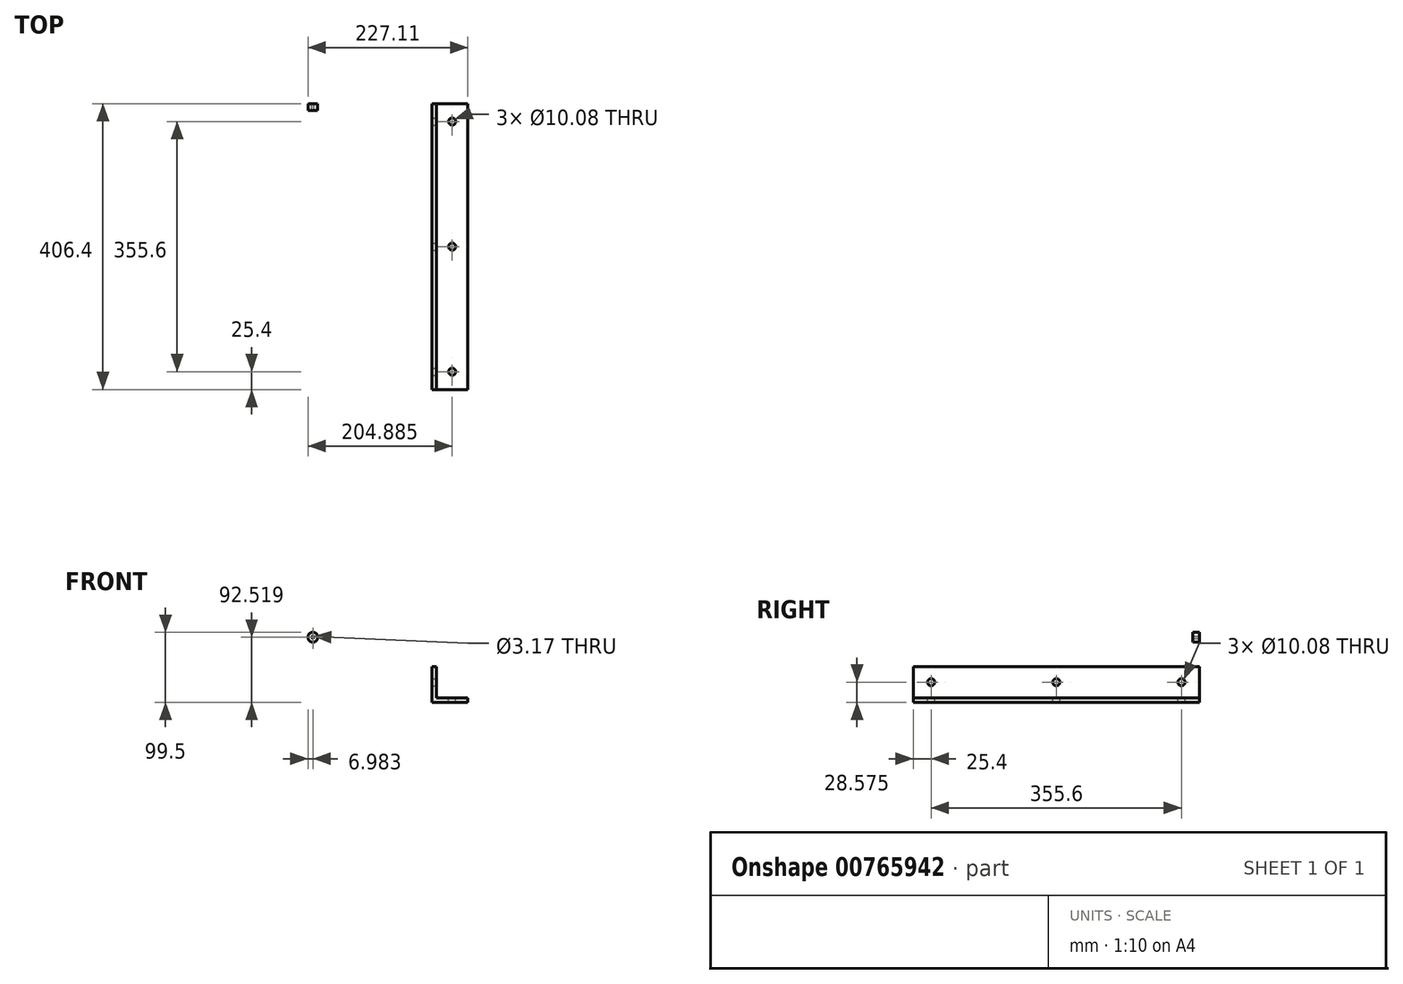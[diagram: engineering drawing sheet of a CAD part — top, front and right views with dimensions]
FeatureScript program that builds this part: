
annotation { "Feature Type Name" : "Feature", "Feature Type Description" : "" }
export const myFeature = defineFeature(function(context is Context, id is Id, definition is map)
    precondition{}
    {
        {
            var Q0;
            Q0=qCreatedBy(makeId("Front.planeOp"),FACE);
            var sketch = newSketch(context, id + "F0", { "sketchPlane" : qUnion([Q0])});
            skLineSegment(sketch, "E0", {"start": v(0, 0) * mm, "end": v(0, 50.8) * mm});
            skLineSegment(sketch, "E1", {"start": v(0, 50.8) * mm, "end": v(0, 50.8) * mm});
            skLineSegment(sketch, "E2", {"start": v(50.8, 6.35) * mm, "end": v(50.8, 0) * mm});
            skLineSegment(sketch, "E3", {"start": v(50.8, 0) * mm, "end": v(0, 0) * mm});
            skLineSegment(sketch, "E4", {"start": v(50.8, 6.35) * mm, "end": v(6.35, 6.35) * mm});
            skLineSegment(sketch, "E5", {"start": v(6.35, 6.35) * mm, "end": v(6.35, 50.8) * mm});
            skLineSegment(sketch, "E6", {"start": v(6.35, 50.8) * mm, "end": v(0, 50.8) * mm});
            skSolve(sketch);
        }
        {
            var Q0;
            Q0 = qSketchRegion(id + "F0", true);
            extrude(context, id + "F1", {"entities" : qUnion([Q0]), "depth" : 406.4 * mm, "offsetDistance" : 25.4 * mm});
        }
        {
            var Q0;
            Q0=makeQuery(id+"F1.opExtrude","SWEPT_FACE",FACE,{"disambiguationData":[OSD([sQuery(id+"F0.wireOp",EDGE,"E5")])]});
            var sketch = newSketch(context, id + "F2", { "sketchPlane" : qUnion([Q0])});
            skLineSegment(sketch, "E7", {"start": v(-406.4, 28.57) * mm, "end": v(0, 28.57) * mm, "construction": true});
            skPoint(sketch, "E8", {"position": v(-381, 28.57) * mm});
            skPoint(sketch, "E9", {"position": v(-25.4, 28.58) * mm});
            skPoint(sketch, "E10", {"position": v(-203.2, 28.57) * mm});
            skSolve(sketch);
        }
        {
            var Q0;
            Q0=makeQuery(id+"F1.opExtrude","SWEPT_FACE",FACE,{"disambiguationData":[OSD([sQuery(id+"F0.wireOp",EDGE,"E4")])]});
            var sketch = newSketch(context, id + "F3", { "sketchPlane" : qUnion([Q0])});
            skLineSegment(sketch, "E11", {"start": v(28.58, 0) * mm, "end": v(28.58, -406.4) * mm, "construction": true});
            skPoint(sketch, "E12", {"position": v(28.58, -381) * mm});
            skPoint(sketch, "E13", {"position": v(28.58, -203.2) * mm});
            skPoint(sketch, "E14", {"position": v(28.58, -25.4) * mm});
            skSolve(sketch);
        }
        {
            var Q0;
            Q0=sQuery(id+"F3.wireOp",VERTEX,"E12");
            var Q1;
            Q1=sQuery(id+"F3.wireOp",VERTEX,"E13");
            var Q2;
            Q2=sQuery(id+"F2.wireOp",VERTEX,"E10");
            var Q3;
            Q3=sQuery(id+"F2.wireOp",VERTEX,"E9");
            var Q4;
            Q4=sQuery(id+"F3.wireOp",VERTEX,"E14");
            var Q5;
            Q5=sQuery(id+"F2.wireOp",VERTEX,"E8");
            var Q6;
            Q6=makeQuery(id+"F1.opExtrude","SWEPT_BODY",BODY,{"disambiguationData":[OSD([sQuery(id+"F0.wireOp",EDGE,"E0"),sQuery(id+"F0.wireOp",EDGE,"E2"),sQuery(id+"F0.wireOp",EDGE,"E3"),sQuery(id+"F0.wireOp",EDGE,"E4"),sQuery(id+"F0.wireOp",EDGE,"E5"),sQuery(id+"F0.wireOp",EDGE,"E6")])]});
            hole(context, id + "F4", {"style" : HoleStyle.SIMPLE, "endStyle" : HoleEndStyle.BLIND, "standardTappedOrClearance" : lookupTablePath({ "standard" : "ANSI", "fit" : "Normal (ASME)", "size" : "3/8", "type" : "Clearance" }), "standardBlindInLast" : lookupTablePath({ "fit" : "Free", "standard" : "ANSI", "size" : "3/8", "type" : "Clearance" }), "holeDiameter" : 10.08 * mm, "majorDiameter" : 6.35 * mm, "holeDepth" : 20.65 * mm, "isTappedThrough" : true, "tappedDepth" : 15.9 * mm, "tapClearance" : 3, "locations" : qUnion([Q0, Q1, Q2, Q3, Q4, Q5]), "scope" : qUnion([Q6])});
        }
        {
            var Q0;
            Q0=qCreatedBy(makeId("Front.planeOp"),FACE);
            var sketch = newSketch(context, id + "F5", { "sketchPlane" : qUnion([Q0])});
            skCircle(sketch, "E15", {"center": v(-169.33, 92.52) * mm, "radius": 6.99 * mm});
            skCircle(sketch, "E16", {"center": v(-169.33, 92.52) * mm, "radius": 1.59 * mm});
            skSolve(sketch);
        }
        {
            var Q0;
            Q0 = qSketchRegion(id + "F5", true);
            extrude(context, id + "F6", {"entities" : qUnion([Q0]), "depth" : 9.35 * mm, "offsetDistance" : 25.4 * mm});
        }
    });
